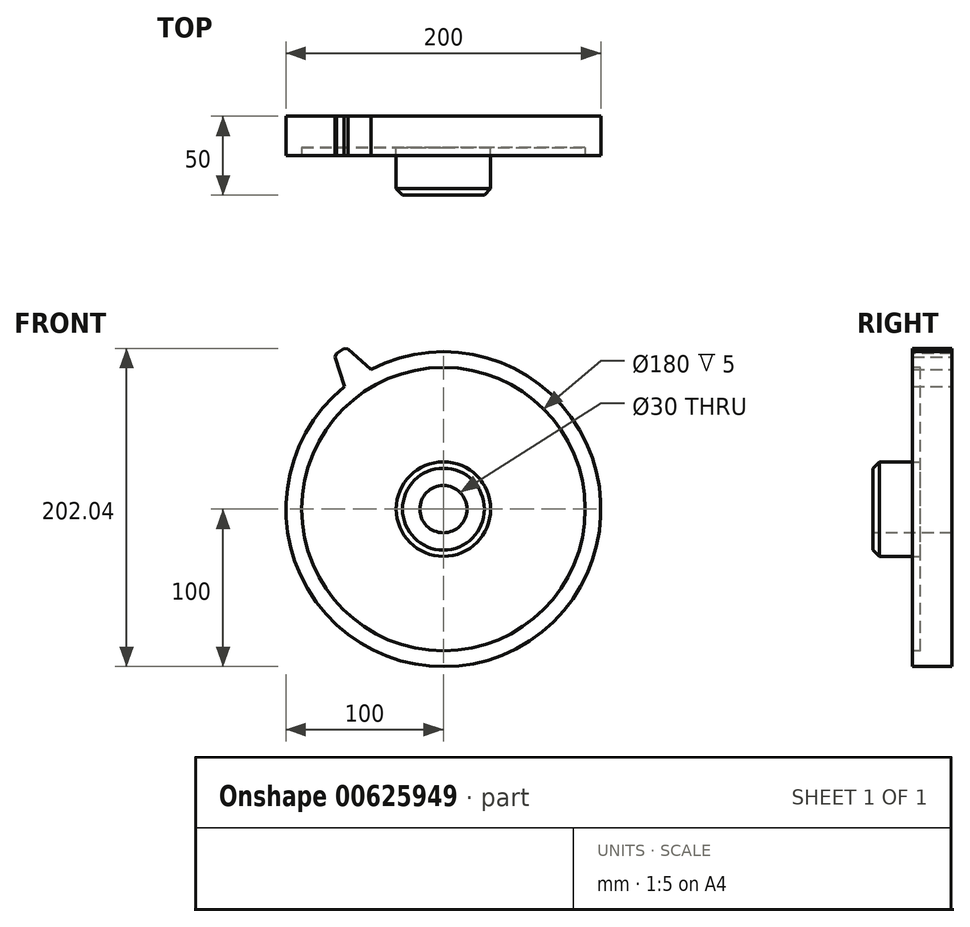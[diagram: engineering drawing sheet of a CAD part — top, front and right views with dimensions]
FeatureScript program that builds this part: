
annotation { "Feature Type Name" : "Feature", "Feature Type Description" : "" }
export const myFeature = defineFeature(function(context is Context, id is Id, definition is map)
    precondition{}
    {
        {
            var Q0;
            Q0=qCreatedBy(makeId("Front.planeOp"),FACE);
            var sketch = newSketch(context, id + "F0", { "sketchPlane" : qUnion([Q0])});
            skCircle(sketch, "E0", {"center": v(0, 0) * mm, "radius": 100 * mm});
            skSolve(sketch);
        }
        {
            var Q0;
            Q0=makeQuery(id+"F0.imprint","IMPRINT",FACE,{"disambiguationData":[TD([[makeQuery(id+"F0.imprint","IMPRINT",EDGE,{"derivedFrom":sQuery(id+"F0.wireOp",EDGE,"E0")}),1.0]])]});
            extrude(context, id + "F1", {"entities" : qUnion([Q0]), "depth" : 25 * mm, "offsetDistance" : 25 * mm});
        }
        {
            var Q0;
            Q0=makeQuery(id+"F1.opExtrude","CAP_FACE",FACE,{"disambiguationData":[OSD([sQuery(id+"F0.wireOp",EDGE,"E0")])],"isStart":false});
            var sketch = newSketch(context, id + "F2", { "sketchPlane" : qUnion([Q0])});
            skCircle(sketch, "E1", {"center": v(0, 0) * mm, "radius": 120 * mm, "construction": true});
            skLineSegment(sketch, "E2", {"start": v(0, 0) * mm, "end": v(-89.9, 137.73) * mm, "construction": true});
            skLineSegment(sketch, "E3", {"start": v(-69.31, 97.96) * mm, "end": v(-62.74, 77.87) * mm});
            skLineSegment(sketch, "E4", {"start": v(-69.31, 97.96) * mm, "end": v(-61.78, 102.88) * mm});
            skLineSegment(sketch, "E5", {"start": v(-62.74, 77.87) * mm, "end": v(-46.04, 88.77) * mm});
            skLineSegment(sketch, "E6.MirrorCS", {"start": v(-61.78, 102.88) * mm, "end": v(-46.04, 88.77) * mm});
            skSolve(sketch);
        }
        {
            var Q0;
            Q0 = qSketchRegion(id + "F2", true);
            var Q1;
            {var subQ0=sQuery(id+"F2.wireOp",EDGE,"E3");Q1=makeQuery(id+"F2.imprint","IMPRINT",FACE,{"disambiguationData":[TD([[makeQuery(id+"F2.imprint","IMPRINT",EDGE,{"derivedFrom":subQ0}),1.0]])]});}
            extrude(context, id + "F3", {"entities" : qUnion([Q0, Q1]), "operationType" : NewBodyOperationType.ADD, "oppositeDirection" : true, "depth" : 25 * mm, "offsetDistance" : 25 * mm});
        }
        {
            var Q0;
            Q0=makeQuery(id+"F3.opExtrude","SWEPT_EDGE",EDGE,{"disambiguationData":[OSD([sQuery(id+"F2.wireOp",EDGE,"E4"),sQuery(id+"F2.wireOp",EDGE,"E6.MirrorCS")])]});
            var Q1;
            Q1=makeQuery(id+"F3.opExtrude","SWEPT_EDGE",EDGE,{"disambiguationData":[OSD([sQuery(id+"F2.wireOp",EDGE,"E3"),sQuery(id+"F2.wireOp",EDGE,"E4")])]});
            chamfer(context, id + "F4", {"entities" : qUnion([Q0, Q1]), "width" : 2 * mm, "tangentPropagation" : true});
        }
        {
            var Q0;
            Q0=makeQuery(id+"F3.opExtrude","SWEPT_EDGE",EDGE,{"disambiguationData":[OSD([sQuery(id+"F0.wireOp",EDGE,"E0"),sQuery(id+"F2.wireOp",EDGE,"E5"),sQuery(id+"F2.wireOp",EDGE,"E6.MirrorCS")])]});
            var Q1;
            Q1=makeQuery(id+"F3.opExtrude","SWEPT_EDGE",EDGE,{"disambiguationData":[OSD([sQuery(id+"F0.wireOp",EDGE,"E0"),sQuery(id+"F2.wireOp",EDGE,"E3"),sQuery(id+"F2.wireOp",EDGE,"E5")])]});
            fillet(context, id + "F5", {"entities" : qUnion([Q0, Q1]), "radius" : 5 * mm, "tangentPropagation" : true, "allowEdgeOverflow" : false});
        }
        {
            var Q0;
            {var subQ0=sQuery(id+"F2.wireOp",EDGE,"E6.MirrorCS");var subQ1=sQuery(id+"F2.wireOp",EDGE,"E5");var subQ2=sQuery(id+"F2.wireOp",EDGE,"E4");var subQ3=sQuery(id+"F2.wireOp",EDGE,"E3");Q0=makeQuery(id+"FnhsdeIWgXpfwR1_1.19.F3.boolean.opBoolean","MERGE",FACE,{"derivedFrom":[makeQuery(id+"FnhsdeIWgXpfwR1_1.18.F3.boolean.opBoolean","MERGE",FACE,{"derivedFrom":[makeQuery(id+"FnhsdeIWgXpfwR1_1.17.F3.boolean.opBoolean","MERGE",FACE,{"derivedFrom":[makeQuery(id+"FnhsdeIWgXpfwR1_1.16.F3.boolean.opBoolean","MERGE",FACE,{"derivedFrom":[makeQuery(id+"FnhsdeIWgXpfwR1_1.15.F3.boolean.opBoolean","MERGE",FACE,{"derivedFrom":[makeQuery(id+"FnhsdeIWgXpfwR1_1.14.F3.boolean.opBoolean","MERGE",FACE,{"derivedFrom":[makeQuery(id+"FnhsdeIWgXpfwR1_1.13.F3.boolean.opBoolean","MERGE",FACE,{"derivedFrom":[makeQuery(id+"FnhsdeIWgXpfwR1_1.12.F3.boolean.opBoolean","MERGE",FACE,{"derivedFrom":[makeQuery(id+"FnhsdeIWgXpfwR1_1.11.F3.boolean.opBoolean","MERGE",FACE,{"derivedFrom":[makeQuery(id+"FnhsdeIWgXpfwR1_1.10.F3.boolean.opBoolean","MERGE",FACE,{"derivedFrom":[makeQuery(id+"FnhsdeIWgXpfwR1_1.9.F3.boolean.opBoolean","MERGE",FACE,{"derivedFrom":[makeQuery(id+"FnhsdeIWgXpfwR1_1.8.F3.boolean.opBoolean","MERGE",FACE,{"derivedFrom":[makeQuery(id+"FnhsdeIWgXpfwR1_1.7.F3.boolean.opBoolean","MERGE",FACE,{"derivedFrom":[makeQuery(id+"FnhsdeIWgXpfwR1_1.6.F3.boolean.opBoolean","MERGE",FACE,{"derivedFrom":[makeQuery(id+"FnhsdeIWgXpfwR1_1.5.F3.boolean.opBoolean","MERGE",FACE,{"derivedFrom":[makeQuery(id+"FnhsdeIWgXpfwR1_1.4.F3.boolean.opBoolean","MERGE",FACE,{"derivedFrom":[makeQuery(id+"FnhsdeIWgXpfwR1_1.3.F3.boolean.opBoolean","MERGE",FACE,{"derivedFrom":[makeQuery(id+"FnhsdeIWgXpfwR1_1.2.F3.boolean.opBoolean","MERGE",FACE,{"derivedFrom":[makeQuery(id+"FnhsdeIWgXpfwR1_1.1.F3.boolean.opBoolean","MERGE",FACE,{"derivedFrom":[makeQuery(id+"F3.boolean.opBoolean","MERGE",FACE,{"derivedFrom":[makeQuery(id+"F1.opExtrude","CAP_FACE",FACE,{"disambiguationData":[OSD([sQuery(id+"F0.wireOp",EDGE,"E0")])],"isStart":false}),makeQuery(id+"F3.opExtrude","CAP_FACE",FACE,{"disambiguationData":[OSD([subQ3,subQ2,subQ1,subQ0])],"isStart":true})]}),makeQuery(id+"FnhsdeIWgXpfwR1_1.1.F3.opExtrude","CAP_FACE",FACE,{"disambiguationData":[OSD([subQ3,subQ2,subQ1,subQ0])],"isStart":true})]}),makeQuery(id+"FnhsdeIWgXpfwR1_1.2.F3.opExtrude","CAP_FACE",FACE,{"disambiguationData":[OSD([subQ3,subQ2,subQ1,subQ0])],"isStart":true})]}),makeQuery(id+"FnhsdeIWgXpfwR1_1.3.F3.opExtrude","CAP_FACE",FACE,{"disambiguationData":[OSD([subQ3,subQ2,subQ1,subQ0])],"isStart":true})]}),makeQuery(id+"FnhsdeIWgXpfwR1_1.4.F3.opExtrude","CAP_FACE",FACE,{"disambiguationData":[OSD([subQ3,subQ2,subQ1,subQ0])],"isStart":true})]}),makeQuery(id+"FnhsdeIWgXpfwR1_1.5.F3.opExtrude","CAP_FACE",FACE,{"disambiguationData":[OSD([subQ3,subQ2,subQ1,subQ0])],"isStart":true})]}),makeQuery(id+"FnhsdeIWgXpfwR1_1.6.F3.opExtrude","CAP_FACE",FACE,{"disambiguationData":[OSD([subQ3,subQ2,subQ1,subQ0])],"isStart":true})]}),makeQuery(id+"FnhsdeIWgXpfwR1_1.7.F3.opExtrude","CAP_FACE",FACE,{"disambiguationData":[OSD([subQ3,subQ2,subQ1,subQ0])],"isStart":true})]}),makeQuery(id+"FnhsdeIWgXpfwR1_1.8.F3.opExtrude","CAP_FACE",FACE,{"disambiguationData":[OSD([subQ3,subQ2,subQ1,subQ0])],"isStart":true})]}),makeQuery(id+"FnhsdeIWgXpfwR1_1.9.F3.opExtrude","CAP_FACE",FACE,{"disambiguationData":[OSD([subQ3,subQ2,subQ1,subQ0])],"isStart":true})]}),makeQuery(id+"FnhsdeIWgXpfwR1_1.10.F3.opExtrude","CAP_FACE",FACE,{"disambiguationData":[OSD([subQ3,subQ2,subQ1,subQ0])],"isStart":true})]}),makeQuery(id+"FnhsdeIWgXpfwR1_1.11.F3.opExtrude","CAP_FACE",FACE,{"disambiguationData":[OSD([subQ3,subQ2,subQ1,subQ0])],"isStart":true})]}),makeQuery(id+"FnhsdeIWgXpfwR1_1.12.F3.opExtrude","CAP_FACE",FACE,{"disambiguationData":[OSD([subQ3,subQ2,subQ1,subQ0])],"isStart":true})]}),makeQuery(id+"FnhsdeIWgXpfwR1_1.13.F3.opExtrude","CAP_FACE",FACE,{"disambiguationData":[OSD([subQ3,subQ2,subQ1,subQ0])],"isStart":true})]}),makeQuery(id+"FnhsdeIWgXpfwR1_1.14.F3.opExtrude","CAP_FACE",FACE,{"disambiguationData":[OSD([subQ3,subQ2,subQ1,subQ0])],"isStart":true})]}),makeQuery(id+"FnhsdeIWgXpfwR1_1.15.F3.opExtrude","CAP_FACE",FACE,{"disambiguationData":[OSD([subQ3,subQ2,subQ1,subQ0])],"isStart":true})]}),makeQuery(id+"FnhsdeIWgXpfwR1_1.16.F3.opExtrude","CAP_FACE",FACE,{"disambiguationData":[OSD([subQ3,subQ2,subQ1,subQ0])],"isStart":true})]}),makeQuery(id+"FnhsdeIWgXpfwR1_1.17.F3.opExtrude","CAP_FACE",FACE,{"disambiguationData":[OSD([subQ3,subQ2,subQ1,subQ0])],"isStart":true})]}),makeQuery(id+"FnhsdeIWgXpfwR1_1.18.F3.opExtrude","CAP_FACE",FACE,{"disambiguationData":[OSD([subQ3,subQ2,subQ1,subQ0])],"isStart":true})]}),makeQuery(id+"FnhsdeIWgXpfwR1_1.19.F3.opExtrude","CAP_FACE",FACE,{"disambiguationData":[OSD([subQ3,subQ2,subQ1,subQ0])],"isStart":true})]});}
            var sketch = newSketch(context, id + "F6", { "sketchPlane" : qUnion([Q0])});
            skCircle(sketch, "E7", {"center": v(0, 0) * mm, "radius": 90 * mm});
            skSolve(sketch);
        }
        {
            var Q0;
            Q0=makeQuery(id+"F6.imprint","IMPRINT",FACE,{"disambiguationData":[TD([[makeQuery(id+"F6.imprint","IMPRINT",EDGE,{"derivedFrom":sQuery(id+"F6.wireOp",EDGE,"E7")}),1.0]])]});
            extrude(context, id + "F7", {"entities" : qUnion([Q0]), "operationType" : NewBodyOperationType.REMOVE, "oppositeDirection" : true, "depth" : 5 * mm, "offsetDistance" : 25 * mm});
        }
        {
            var Q0;
            Q0=makeQuery(id+"F7.boolean.opBoolean","COPY",FACE,{"derivedFrom":makeQuery(id+"F7.opExtrude","CAP_FACE",FACE,{"disambiguationData":[OSD([sQuery(id+"F6.wireOp",EDGE,"E7")])],"isStart":false})});
            var sketch = newSketch(context, id + "F8", { "sketchPlane" : qUnion([Q0])});
            skCircle(sketch, "E8", {"center": v(0, 0) * mm, "radius": 30 * mm});
            skSolve(sketch);
        }
        {
            var Q0;
            Q0=makeQuery(id+"F8.imprint","IMPRINT",FACE,{"disambiguationData":[TD([[makeQuery(id+"F8.imprint","IMPRINT",EDGE,{"derivedFrom":sQuery(id+"F8.wireOp",EDGE,"E8")}),1.0]])]});
            extrude(context, id + "F9", {"entities" : qUnion([Q0]), "operationType" : NewBodyOperationType.ADD, "depth" : 30 * mm, "offsetDistance" : 25 * mm});
        }
        {
            var Q0;
            Q0=makeQuery(id+"F9.opExtrude","CAP_FACE",FACE,{"disambiguationData":[OSD([sQuery(id+"F8.wireOp",EDGE,"E8")])],"isStart":false});
            var sketch = newSketch(context, id + "F10", { "sketchPlane" : qUnion([Q0])});
            skCircle(sketch, "E9", {"center": v(0, 0) * mm, "radius": 15 * mm});
            skSolve(sketch);
        }
        {
            var Q0;
            Q0=makeQuery(id+"F10.imprint","IMPRINT",FACE,{"disambiguationData":[TD([[makeQuery(id+"F10.imprint","IMPRINT",EDGE,{"derivedFrom":sQuery(id+"F10.wireOp",EDGE,"E9")}),1.0]])]});
            extrude(context, id + "F11", {"entities" : qUnion([Q0]), "operationType" : NewBodyOperationType.REMOVE, "endBound" : BoundingType.THROUGH_ALL, "oppositeDirection" : true, "depth" : 25 * mm, "offsetDistance" : 25 * mm});
        }
        {
            var Q0;
            Q0=makeQuery(id+"F11.boolean.opBoolean","COPY",EDGE,{"derivedFrom":makeQuery(id+"F11.opExtrude","CAP_EDGE",EDGE,{"disambiguationData":[OSD([sQuery(id+"F10.wireOp",EDGE,"E9")])],"isStart":true})});
            var Q1;
            Q1=makeQuery(id+"F9.opExtrude","CAP_EDGE",EDGE,{"disambiguationData":[OSD([sQuery(id+"F8.wireOp",EDGE,"E8")])],"isStart":false});
            chamfer(context, id + "F12", {"entities" : qUnion([Q0, Q1]), "width" : 4 * mm, "tangentPropagation" : true});
        }
    });
